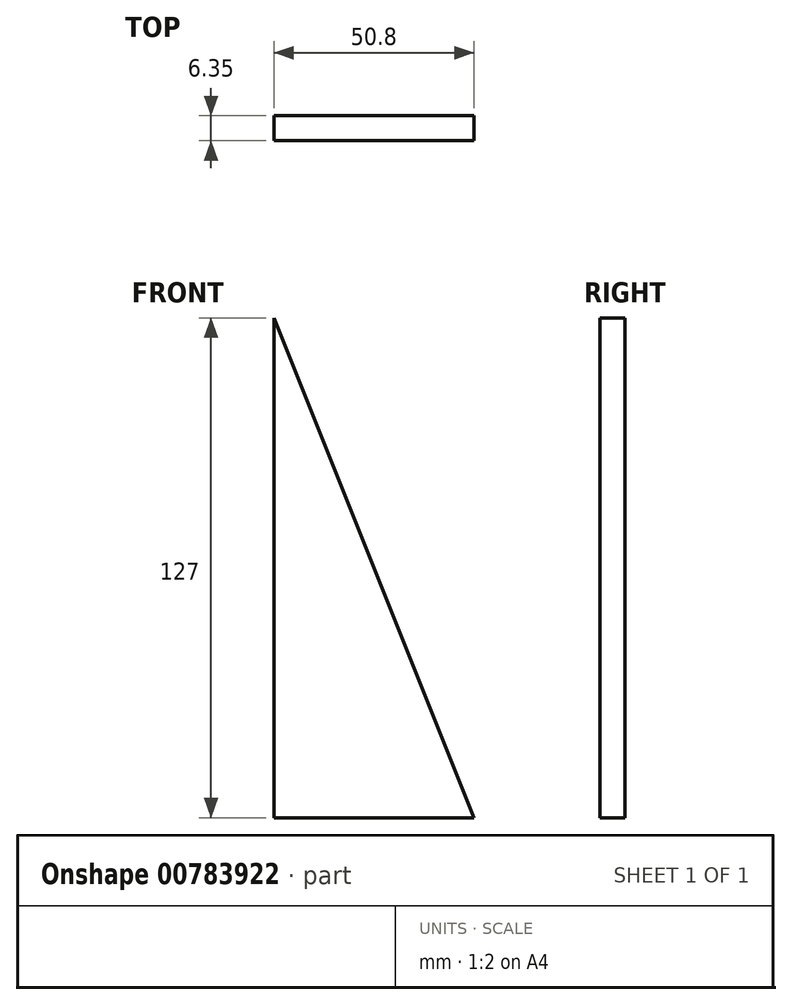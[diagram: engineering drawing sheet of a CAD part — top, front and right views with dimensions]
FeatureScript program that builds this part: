
annotation { "Feature Type Name" : "Feature", "Feature Type Description" : "" }
export const myFeature = defineFeature(function(context is Context, id is Id, definition is map)
    precondition{}
    {
        {
            var Q0;
            Q0=qCreatedBy(makeId("Front.planeOp"),FACE);
            var sketch = newSketch(context, id + "F0", { "sketchPlane" : qUnion([Q0])});
            skLineSegment(sketch, "E0.bottom", {"start": v(0, 0) * mm, "end": v(50.8, 0) * mm});
            skLineSegment(sketch, "E0.left", {"start": v(0, 0) * mm, "end": v(0, 127) * mm});
            skLineSegment(sketch, "E1", {"start": v(0, 127) * mm, "end": v(50.8, 0) * mm});
            skSolve(sketch);
        }
        {
            var Q0;
            Q0=makeQuery(id+"F0.imprint","IMPRINT",FACE,{"disambiguationData":[TD([[makeQuery(id+"F0.imprint","IMPRINT",EDGE,{"derivedFrom":sQuery(id+"F0.wireOp",EDGE,"E0.bottom")}),1.0]])]});
            extrude(context, id + "F1", {"entities" : qUnion([Q0]), "depth" : 6.35 * mm, "offsetDistance" : 25.4 * mm});
        }
    });
